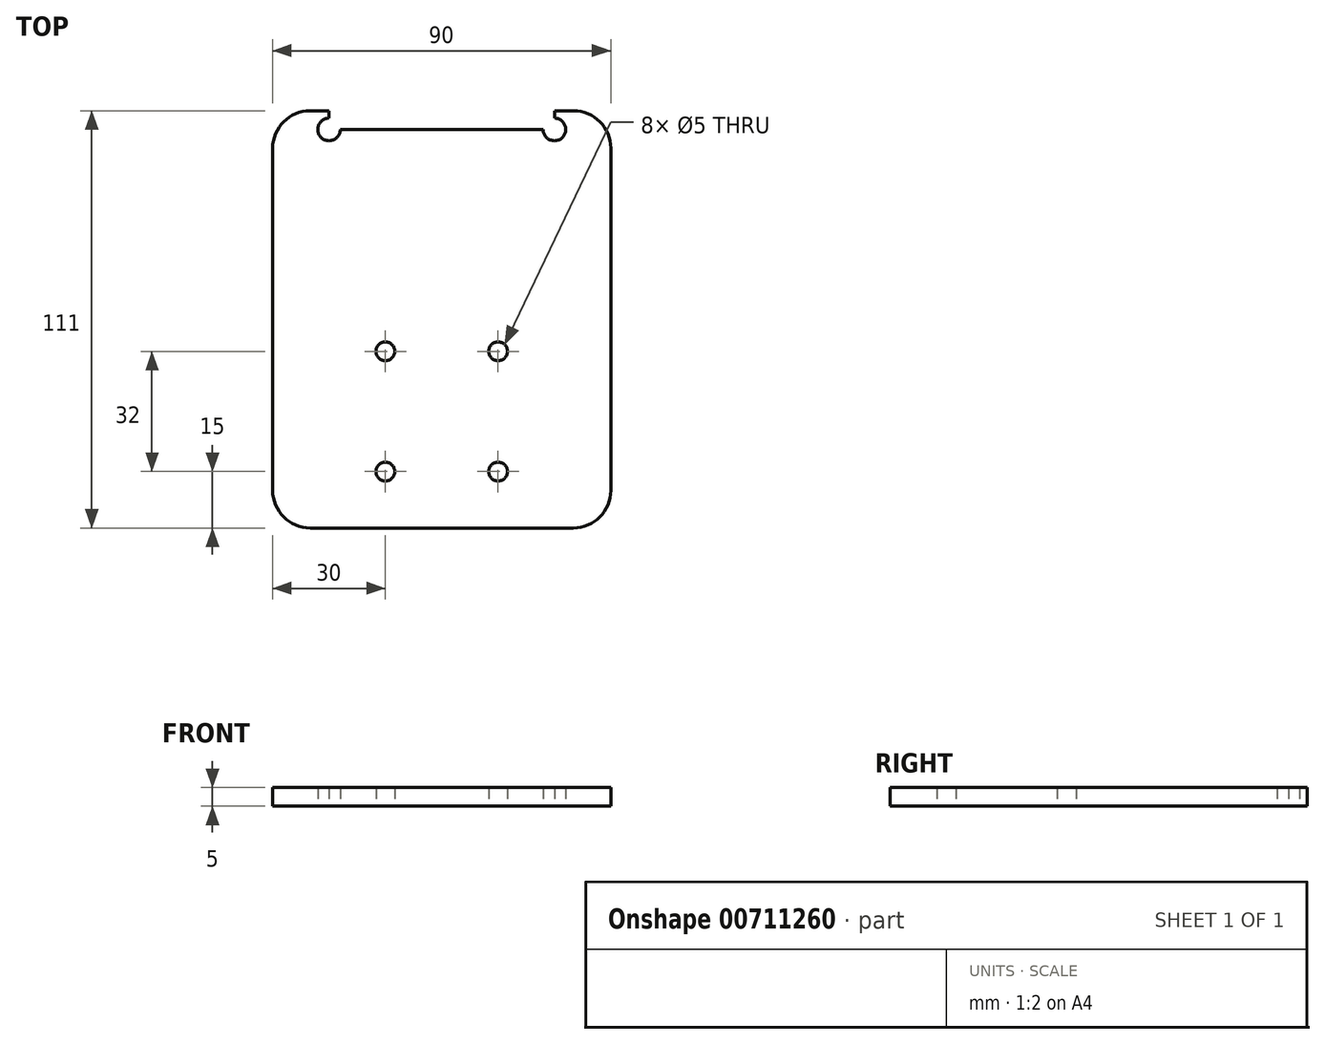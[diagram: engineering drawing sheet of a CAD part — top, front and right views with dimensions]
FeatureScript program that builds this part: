
annotation { "Feature Type Name" : "Feature", "Feature Type Description" : "" }
export const myFeature = defineFeature(function(context is Context, id is Id, definition is map)
    precondition{}
    {
        {
            var Q0;
            Q0=qCreatedBy(makeId("Top.planeOp"),FACE);
            var sketch = newSketch(context, id + "F0", { "sketchPlane" : qUnion([Q0])});
            skPoint(sketch, "E0.middle", {"position": v(0, 0) * mm});
            skCircle(sketch, "E1", {"center": v(-15, -10.5) * mm, "radius": 2.5 * mm});
            skCircle(sketch, "E2", {"center": v(-15, -42.5) * mm, "radius": 2.5 * mm});
            skCircle(sketch, "E3", {"center": v(15, -10.5) * mm, "radius": 2.5 * mm});
            skCircle(sketch, "E4", {"center": v(15, -42.5) * mm, "radius": 2.5 * mm});
            skLineSegment(sketch, "E5.top", {"start": v(35, -57.5) * mm, "end": v(-35, -57.5) * mm});
            skLineSegment(sketch, "E5.left", {"start": v(45, 43.5) * mm, "end": v(45, -47.5) * mm});
            skLineSegment(sketch, "E5.right", {"start": v(-45, 43.5) * mm, "end": v(-45, -47.5) * mm});
            skPoint(sketch, "E6.visualSharp", {"position": v(-45, 57.5) * mm});
            skArc(sketch, "E6.filletArc", {"start": v(-35, 53.5) * mm, "mid": v(-42.07, 50.57) * mm, "end": v(-45, 43.5) * mm});
            skPoint(sketch, "E7.visualSharp", {"position": v(45, 57.5) * mm});
            skArc(sketch, "E7.filletArc", {"start": v(45, 43.5) * mm, "mid": v(42.07, 50.57) * mm, "end": v(35, 53.5) * mm});
            skPoint(sketch, "E8.visualSharp", {"position": v(45, -57.5) * mm});
            skArc(sketch, "E8.filletArc", {"start": v(35, -57.5) * mm, "mid": v(42.07, -54.57) * mm, "end": v(45, -47.5) * mm});
            skPoint(sketch, "E9.visualSharp", {"position": v(-45, -57.5) * mm});
            skArc(sketch, "E9.filletArc", {"start": v(-45, -47.5) * mm, "mid": v(-42.07, -54.57) * mm, "end": v(-35, -57.5) * mm});
            skLineSegment(sketch, "E10", {"start": v(-35, 53.5) * mm, "end": v(-30, 53.5) * mm});
            skLineSegment(sketch, "E11.0", {"start": v(-27, 48.5) * mm, "end": v(27, 48.5) * mm});
            skLineSegment(sketch, "E12.0", {"start": v(30, 51.5) * mm, "end": v(30, 53.5) * mm});
            skLineSegment(sketch, "E13.0", {"start": v(-30, 51.5) * mm, "end": v(-30, 53.5) * mm});
            skPoint(sketch, "E14.orphan", {"position": v(-35, 48.5) * mm});
            skPoint(sketch, "E15.orphan", {"position": v(35, 48.5) * mm});
            skLineSegment(sketch, "E16.trimOffspring", {"start": v(30, 53.5) * mm, "end": v(35, 53.5) * mm});
            skArc(sketch, "E17", {"start": v(-30, 51.5) * mm, "mid": v(-32.12, 46.38) * mm, "end": v(-27, 48.5) * mm});
            skArc(sketch, "E18", {"start": v(27, 48.5) * mm, "mid": v(32.12, 46.38) * mm, "end": v(30, 51.5) * mm});
            skSolve(sketch);
        }
        {
            var Q0;
            Q0=makeQuery(id+"F0.imprint","IMPRINT",FACE,{"disambiguationData":[TD([[makeQuery(id+"F0.imprint","IMPRINT",EDGE,{"derivedFrom":sQuery(id+"F0.wireOp",EDGE,"E1")}),-1.0]])]});
            extrude(context, id + "F1", {"entities" : qUnion([Q0]), "depth" : 5 * mm, "offsetDistance" : 25 * mm});
        }
    });
